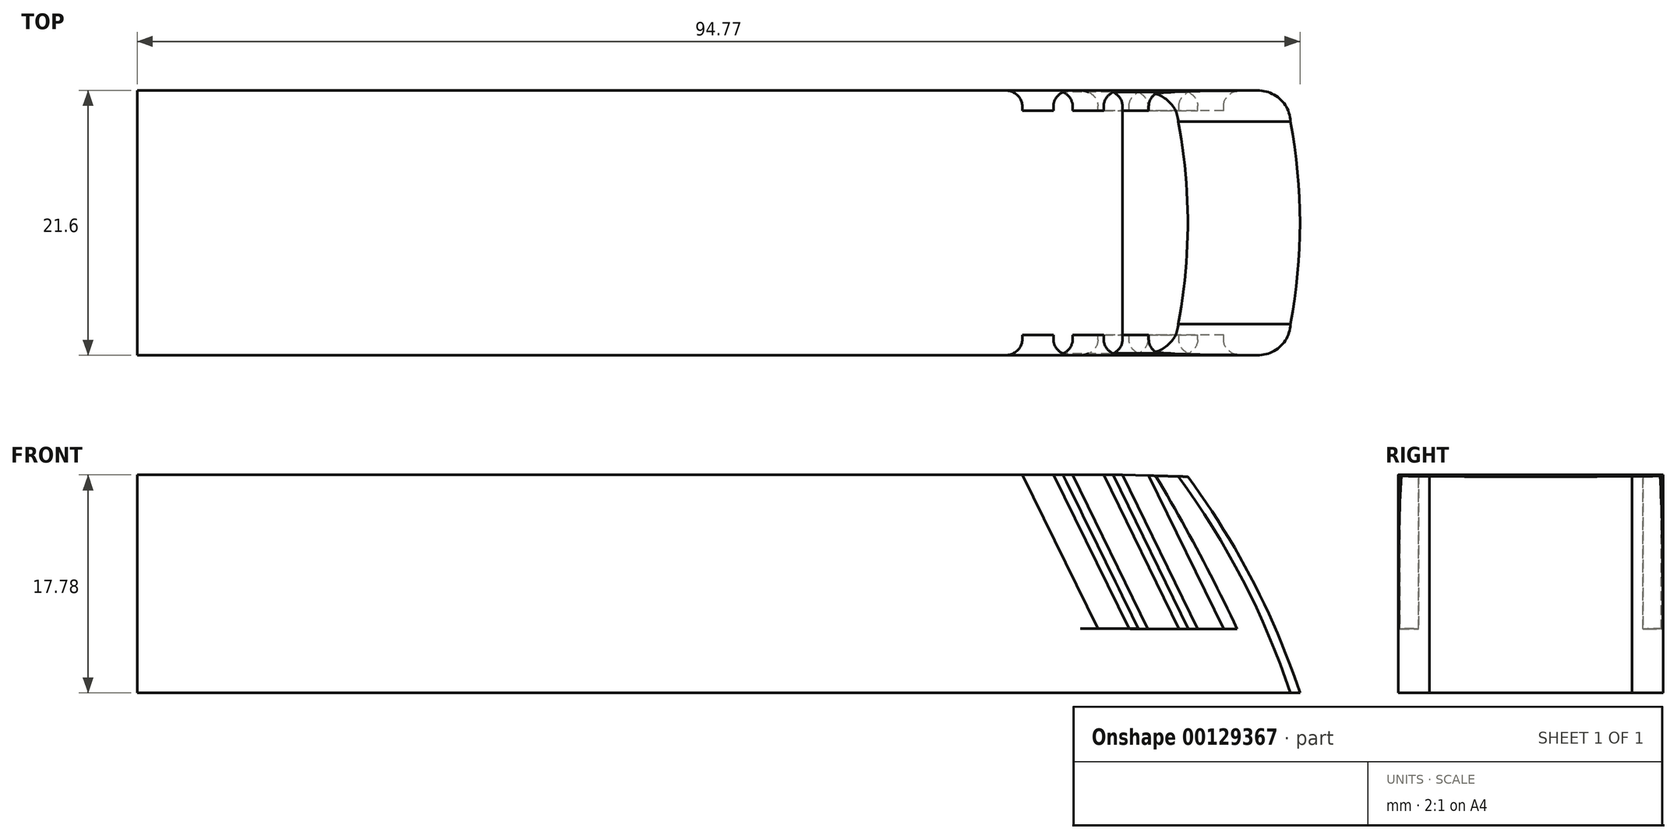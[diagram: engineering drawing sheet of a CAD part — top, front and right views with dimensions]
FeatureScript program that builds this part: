
annotation { "Feature Type Name" : "Feature", "Feature Type Description" : "" }
export const myFeature = defineFeature(function(context is Context, id is Id, definition is map)
    precondition{}
    {
        {
            var Q0;
            Q0=qCreatedBy(makeId("Front.planeOp"),FACE);
            var sketch = newSketch(context, id + "F0", { "sketchPlane" : qUnion([Q0])});
            skLineSegment(sketch, "E0", {"start": v(-54.59, -17.6) * mm, "end": v(-54.59, 0.19) * mm});
            skLineSegment(sketch, "E1", {"start": v(-54.59, -17.6) * mm, "end": v(39.4, -17.6) * mm});
            skLineSegment(sketch, "E2", {"start": v(-54.59, 0.19) * mm, "end": v(25.72, 0.19) * mm});
            skLineSegment(sketch, "E3.0", {"start": v(33.96, -12.37) * mm, "end": v(27.71, 0.43) * mm});
            skLineSegment(sketch, "E4", {"start": v(25.72, 0.19) * mm, "end": v(31.84, -12.37) * mm});
            skLineSegment(sketch, "E5", {"start": v(33.96, -12.37) * mm, "end": v(31.84, -12.37) * mm});
            skLineSegment(sketch, "E6", {"start": v(24.2, 0.19) * mm, "end": v(30.32, -12.37) * mm});
            skLineSegment(sketch, "E7", {"start": v(30.32, -12.37) * mm, "end": v(27.78, -12.37) * mm});
            skLineSegment(sketch, "E8", {"start": v(27.78, -12.37) * mm, "end": v(21.65, 0.19) * mm});
            skLineSegment(sketch, "E9", {"start": v(20.1, 0.19) * mm, "end": v(26.26, -12.35) * mm});
            skLineSegment(sketch, "E10", {"start": v(17.55, 0.19) * mm, "end": v(23.72, -12.35) * mm});
            skLineSegment(sketch, "E11", {"start": v(26.26, -12.35) * mm, "end": v(23.72, -12.35) * mm});
            skLineSegment(sketch, "E12", {"start": v(30.25, 0.06) * mm, "end": v(25.72, 0.19) * mm});
            skLineSegment(sketch, "E13", {"start": v(30.25, 0.06) * mm, "end": v(39.4, -17.6) * mm});
            skArc(sketch, "E14", {"start": v(39.4, -17.6) * mm, "mid": v(35.52, -8.4) * mm, "end": v(30.25, 0.06) * mm});
            skSolve(sketch);
        }
        {
            var Q0;
            {var subQ6=sQuery(id+"F0.wireOp",EDGE,"E0");Q0=makeQuery(id+"F0.imprint","IMPRINT",FACE,{"disambiguationData":[TD([[makeQuery(id+"F0.imprint","IMPRINT",EDGE,{"derivedFrom":subQ6}),-1.0]])]});}
            var Q1;
            Q1=makeQuery(id+"F0.imprint","IMPRINT",FACE,{"disambiguationData":[TD([[makeQuery(id+"F0.imprint","IMPRINT",EDGE,{"derivedFrom":sQuery(id+"F0.wireOp",EDGE,"657433ce-35f6-41b5-b99d-85d71bb0a3c1")}),-1.0]])]});
            var Q2;
            Q2=makeQuery(id+"F0.imprint","IMPRINT",FACE,{"disambiguationData":[TD([[makeQuery(id+"F0.imprint","IMPRINT",EDGE,{"derivedFrom":sQuery(id+"F0.wireOp",EDGE,"E13")}),1.0]])]});
            extrude(context, id + "F1", {"entities" : qUnion([Q0, Q1, Q2]), "depth" : 21.59 * mm, "symmetric" : true});
        }
        {
            var Q0;
            {var subQ0=sQuery(id+"F0.wireOp",EDGE,"E9");Q0=makeQuery(id+"F0.imprint","IMPRINT",FACE,{"disambiguationData":[TD([[makeQuery(id+"F0.imprint","IMPRINT",EDGE,{"derivedFrom":subQ0}),-1.0]])]});}
            var Q1;
            {var subQ0=sQuery(id+"F0.wireOp",EDGE,"E6");Q1=makeQuery(id+"F0.imprint","IMPRINT",FACE,{"disambiguationData":[TD([[makeQuery(id+"F0.imprint","IMPRINT",EDGE,{"derivedFrom":subQ0}),-1.0]])]});}
            var Q2;
            {var subQ4=sQuery(id+"F0.wireOp",EDGE,"E4");Q2=makeQuery(id+"F0.imprint","IMPRINT",FACE,{"disambiguationData":[TD([[makeQuery(id+"F0.imprint","IMPRINT",EDGE,{"derivedFrom":subQ4}),1.0]])]});}
            extrude(context, id + "F2", {"entities" : qUnion([Q0, Q1, Q2]), "operationType" : NewBodyOperationType.ADD, "depth" : 18.29 * mm, "symmetric" : true});
        }
        {
            var Q0;
            Q0=makeQuery(id+"F1.opExtrude","CAP_EDGE",EDGE,{"disambiguationData":[OSD([sQuery(id+"F0.wireOp",EDGE,"E10")])],"isStart":false});
            var Q1;
            Q1=makeQuery(id+"F1.opExtrude","CAP_EDGE",EDGE,{"disambiguationData":[OSD([sQuery(id+"F0.wireOp",EDGE,"E9")])],"isStart":false});
            var Q2;
            Q2=makeQuery(id+"F1.opExtrude","CAP_EDGE",EDGE,{"disambiguationData":[OSD([sQuery(id+"F0.wireOp",EDGE,"E8")])],"isStart":false});
            var Q3;
            Q3=makeQuery(id+"F1.opExtrude","CAP_EDGE",EDGE,{"disambiguationData":[OSD([sQuery(id+"F0.wireOp",EDGE,"E6")])],"isStart":false});
            var Q4;
            Q4=makeQuery(id+"F1.opExtrude","CAP_EDGE",EDGE,{"disambiguationData":[OSD([sQuery(id+"F0.wireOp",EDGE,"657433ce-35f6-41b5-b99d-85d71bb0a3c1")])],"isStart":false});
            var Q5;
            Q5=makeQuery(id+"F1.opExtrude","CAP_EDGE",EDGE,{"disambiguationData":[OSD([sQuery(id+"F0.wireOp",EDGE,"E3.0")])],"isStart":false});
            fillet(context, id + "F3", {"entities" : qUnion([Q0, Q1, Q2, Q3, Q4, Q5]), "radius" : 1.27 * mm, "tangentPropagation" : true, "allowEdgeOverflow" : false});
        }
        {
            var Q0;
            {var subQ0=sQuery(id+"F0.wireOp",EDGE,"E6");Q0=makeQuery(id+"F3.opFillet","BLEND_EDGE",EDGE,{"blendedFrom":[makeQuery(id+"F1.opExtrude","CAP_EDGE",EDGE,{"disambiguationData":[OSD([subQ0])],"isStart":false}),makeQuery(id+"F1.opExtrude","CAP_FACE",FACE,{"disambiguationData":[OSD([sQuery(id+"F0.wireOp",EDGE,"E0"),sQuery(id+"F0.wireOp",EDGE,"E1"),sQuery(id+"F0.wireOp",EDGE,"E2"),sQuery(id+"F0.wireOp",EDGE,"E3.0"),sQuery(id+"F0.wireOp",EDGE,"E4"),sQuery(id+"F0.wireOp",EDGE,"E5"),subQ0,sQuery(id+"F0.wireOp",EDGE,"E7"),sQuery(id+"F0.wireOp",EDGE,"E8"),sQuery(id+"F0.wireOp",EDGE,"E9"),sQuery(id+"F0.wireOp",EDGE,"E10"),sQuery(id+"F0.wireOp",EDGE,"E11"),sQuery(id+"F0.wireOp",EDGE,"657433ce-35f6-41b5-b99d-85d71bb0a3c1"),sQuery(id+"F0.wireOp",EDGE,"E12")])],"isStart":false})],"blendedInto":[makeQuery(id+"F1.opExtrude","CAP_FACE",FACE,{"disambiguationData":[OSD([sQuery(id+"F0.wireOp",EDGE,"E0"),sQuery(id+"F0.wireOp",EDGE,"E1"),sQuery(id+"F0.wireOp",EDGE,"E2"),sQuery(id+"F0.wireOp",EDGE,"E3.0"),sQuery(id+"F0.wireOp",EDGE,"E4"),sQuery(id+"F0.wireOp",EDGE,"E5"),subQ0,sQuery(id+"F0.wireOp",EDGE,"E7"),sQuery(id+"F0.wireOp",EDGE,"E8"),sQuery(id+"F0.wireOp",EDGE,"E9"),sQuery(id+"F0.wireOp",EDGE,"E10"),sQuery(id+"F0.wireOp",EDGE,"E11"),sQuery(id+"F0.wireOp",EDGE,"657433ce-35f6-41b5-b99d-85d71bb0a3c1"),sQuery(id+"F0.wireOp",EDGE,"E12")])],"isStart":false})]});}
            var Q1;
            Q1=makeQuery(id+"F1.opExtrude","CAP_EDGE",EDGE,{"disambiguationData":[OSD([sQuery(id+"F0.wireOp",EDGE,"E4")])],"isStart":false});
            fillet(context, id + "F4", {"entities" : qUnion([Q0, Q1]), "radius" : 1.27 * mm, "tangentPropagation" : true, "allowEdgeOverflow" : false});
        }
        {
            var Q0;
            Q0=makeQuery(id+"F1.opExtrude","CAP_EDGE",EDGE,{"disambiguationData":[OSD([sQuery(id+"F0.wireOp",EDGE,"E10")])],"isStart":true});
            var Q1;
            Q1=makeQuery(id+"F1.opExtrude","CAP_EDGE",EDGE,{"disambiguationData":[OSD([sQuery(id+"F0.wireOp",EDGE,"E9")])],"isStart":true});
            var Q2;
            Q2=makeQuery(id+"F1.opExtrude","CAP_EDGE",EDGE,{"disambiguationData":[OSD([sQuery(id+"F0.wireOp",EDGE,"E6")])],"isStart":true});
            var Q3;
            Q3=makeQuery(id+"F1.opExtrude","CAP_EDGE",EDGE,{"disambiguationData":[OSD([sQuery(id+"F0.wireOp",EDGE,"E3.0")])],"isStart":true});
            var Q4;
            Q4=makeQuery(id+"F1.opExtrude","CAP_EDGE",EDGE,{"disambiguationData":[OSD([sQuery(id+"F0.wireOp",EDGE,"657433ce-35f6-41b5-b99d-85d71bb0a3c1")])],"isStart":true});
            fillet(context, id + "F5", {"entities" : qUnion([Q0, Q1, Q2, Q3, Q4]), "radius" : 1.27 * mm, "tangentPropagation" : true, "allowEdgeOverflow" : false});
        }
        {
            var Q0;
            {var subQ0=sQuery(id+"F0.wireOp",EDGE,"E6");Q0=makeQuery(id+"F5.opFillet","BLEND_EDGE",EDGE,{"blendedFrom":[makeQuery(id+"F1.opExtrude","CAP_EDGE",EDGE,{"disambiguationData":[OSD([subQ0])],"isStart":true}),makeQuery(id+"F1.opExtrude","CAP_FACE",FACE,{"disambiguationData":[OSD([sQuery(id+"F0.wireOp",EDGE,"E0"),sQuery(id+"F0.wireOp",EDGE,"E1"),sQuery(id+"F0.wireOp",EDGE,"E2"),sQuery(id+"F0.wireOp",EDGE,"E3.0"),sQuery(id+"F0.wireOp",EDGE,"E4"),sQuery(id+"F0.wireOp",EDGE,"E5"),subQ0,sQuery(id+"F0.wireOp",EDGE,"E7"),sQuery(id+"F0.wireOp",EDGE,"E8"),sQuery(id+"F0.wireOp",EDGE,"E9"),sQuery(id+"F0.wireOp",EDGE,"E10"),sQuery(id+"F0.wireOp",EDGE,"E11"),sQuery(id+"F0.wireOp",EDGE,"657433ce-35f6-41b5-b99d-85d71bb0a3c1"),sQuery(id+"F0.wireOp",EDGE,"E12")])],"isStart":true})],"blendedInto":[makeQuery(id+"F1.opExtrude","CAP_FACE",FACE,{"disambiguationData":[OSD([sQuery(id+"F0.wireOp",EDGE,"E0"),sQuery(id+"F0.wireOp",EDGE,"E1"),sQuery(id+"F0.wireOp",EDGE,"E2"),sQuery(id+"F0.wireOp",EDGE,"E3.0"),sQuery(id+"F0.wireOp",EDGE,"E4"),sQuery(id+"F0.wireOp",EDGE,"E5"),subQ0,sQuery(id+"F0.wireOp",EDGE,"E7"),sQuery(id+"F0.wireOp",EDGE,"E8"),sQuery(id+"F0.wireOp",EDGE,"E9"),sQuery(id+"F0.wireOp",EDGE,"E10"),sQuery(id+"F0.wireOp",EDGE,"E11"),sQuery(id+"F0.wireOp",EDGE,"657433ce-35f6-41b5-b99d-85d71bb0a3c1"),sQuery(id+"F0.wireOp",EDGE,"E12")])],"isStart":true})]});}
            var Q1;
            Q1=makeQuery(id+"F1.opExtrude","CAP_EDGE",EDGE,{"disambiguationData":[OSD([sQuery(id+"F0.wireOp",EDGE,"E4")])],"isStart":true});
            var Q2;
            Q2=makeQuery(id+"F1.opExtrude","CAP_EDGE",EDGE,{"disambiguationData":[OSD([sQuery(id+"F0.wireOp",EDGE,"E8")])],"isStart":true});
            var Q3;
            {var subQ0=sQuery(id+"F0.wireOp",EDGE,"E9");Q3=makeQuery(id+"F5.opFillet","BLEND_EDGE",EDGE,{"blendedFrom":[makeQuery(id+"F1.opExtrude","CAP_EDGE",EDGE,{"disambiguationData":[OSD([subQ0])],"isStart":true}),makeQuery(id+"F1.opExtrude","CAP_FACE",FACE,{"disambiguationData":[OSD([sQuery(id+"F0.wireOp",EDGE,"E0"),sQuery(id+"F0.wireOp",EDGE,"E1"),sQuery(id+"F0.wireOp",EDGE,"E2"),sQuery(id+"F0.wireOp",EDGE,"E3.0"),sQuery(id+"F0.wireOp",EDGE,"E4"),sQuery(id+"F0.wireOp",EDGE,"E5"),sQuery(id+"F0.wireOp",EDGE,"E6"),sQuery(id+"F0.wireOp",EDGE,"E7"),sQuery(id+"F0.wireOp",EDGE,"E8"),subQ0,sQuery(id+"F0.wireOp",EDGE,"E10"),sQuery(id+"F0.wireOp",EDGE,"E11"),sQuery(id+"F0.wireOp",EDGE,"657433ce-35f6-41b5-b99d-85d71bb0a3c1"),sQuery(id+"F0.wireOp",EDGE,"E12")])],"isStart":true})],"blendedInto":[makeQuery(id+"F1.opExtrude","CAP_FACE",FACE,{"disambiguationData":[OSD([sQuery(id+"F0.wireOp",EDGE,"E0"),sQuery(id+"F0.wireOp",EDGE,"E1"),sQuery(id+"F0.wireOp",EDGE,"E2"),sQuery(id+"F0.wireOp",EDGE,"E3.0"),sQuery(id+"F0.wireOp",EDGE,"E4"),sQuery(id+"F0.wireOp",EDGE,"E5"),sQuery(id+"F0.wireOp",EDGE,"E6"),sQuery(id+"F0.wireOp",EDGE,"E7"),sQuery(id+"F0.wireOp",EDGE,"E8"),subQ0,sQuery(id+"F0.wireOp",EDGE,"E10"),sQuery(id+"F0.wireOp",EDGE,"E11"),sQuery(id+"F0.wireOp",EDGE,"657433ce-35f6-41b5-b99d-85d71bb0a3c1"),sQuery(id+"F0.wireOp",EDGE,"E12")])],"isStart":true})]});}
            fillet(context, id + "F6", {"entities" : qUnion([Q0, Q1, Q2, Q3]), "radius" : 1.27 * mm, "tangentPropagation" : true, "allowEdgeOverflow" : false});
        }
        {
            var Q0;
            Q0=makeQuery(id+"F1.opExtrude","CAP_EDGE",EDGE,{"disambiguationData":[OSD([sQuery(id+"F0.wireOp",EDGE,"E14")])],"isStart":false});
            var Q1;
            Q1=makeQuery(id+"F1.opExtrude","CAP_EDGE",EDGE,{"disambiguationData":[OSD([sQuery(id+"F0.wireOp",EDGE,"E14")])],"isStart":true});
            fillet(context, id + "F7", {"entities" : qUnion([Q0, Q1]), "radius" : 2.54 * mm, "allowEdgeOverflow" : false});
        }
        {
            var Q0;
            {var subQ0=sQuery(id+"F0.wireOp",EDGE,"E12");Q0=makeQuery(id+"F2.boolean.opBoolean","MERGE",FACE,{"derivedFrom":[makeQuery(id+"F1.opExtrude","SWEPT_FACE",FACE,{"disambiguationData":[OSD([subQ0])]}),makeQuery(id+"F2.opExtrude","SWEPT_FACE",FACE,{"disambiguationData":[OSD([subQ0])]})]});}
            cPlane(context, id + "F8", {"entities" : qUnion([Q0]), "cplaneType" : CPlaneType.OFFSET, "offset" : 0 * mm, "width" : 152.4 * mm, "height" : 152.4 * mm});
        }
        {
            var Q0;
            Q0=qCreatedBy(id+"F8.planeOp",FACE);
            var sketch = newSketch(context, id + "F9", { "sketchPlane" : qUnion([Q0])});
            skLineSegment(sketch, "E15", {"start": v(30.24, 8.26) * mm, "end": v(30.24, -8.26) * mm});
            skArc(sketch, "E16", {"start": v(30.24, -8.26) * mm, "mid": v(31.03, 0) * mm, "end": v(30.24, 8.26) * mm});
            skSolve(sketch);
        }
        {
            var Q0;
            Q0=makeQuery(id+"F1.opExtrude","SWEPT_FACE",FACE,{"disambiguationData":[OSD([sQuery(id+"F0.wireOp",EDGE,"E1")])]});
            cPlane(context, id + "F10", {"entities" : qUnion([Q0]), "cplaneType" : CPlaneType.OFFSET, "offset" : 0 * mm, "width" : 152.4 * mm, "height" : 152.4 * mm});
        }
        {
            var Q0;
            Q0=qCreatedBy(id+"F10.planeOp",FACE);
            var sketch = newSketch(context, id + "F11", { "sketchPlane" : qUnion([Q0])});
            skLineSegment(sketch, "E17", {"start": v(39.4, 8.26) * mm, "end": v(39.4, -8.26) * mm});
            skArc(sketch, "E18", {"start": v(39.4, -8.25) * mm, "mid": v(40.18, 0) * mm, "end": v(39.4, 8.25) * mm});
            skSolve(sketch);
        }
        {
            var Q1;
            Q1=makeQuery(id+"F9.imprint","IMPRINT",FACE,{"disambiguationData":[TD([[makeQuery(id+"F9.imprint","IMPRINT",EDGE,{"derivedFrom":sQuery(id+"F9.wireOp",EDGE,"E15")}),1.0]])]});
            var Q2;
            Q2=makeQuery(id+"F11.imprint","IMPRINT",FACE,{"disambiguationData":[TD([[makeQuery(id+"F11.imprint","IMPRINT",EDGE,{"derivedFrom":sQuery(id+"F11.wireOp",EDGE,"E17")}),1.0]])]});
            var Q3;
            {var subQ0=sQuery(id+"F0.wireOp",EDGE,"E14");Q3=makeQuery(id+"F7.opFillet","BLEND_EDGE",EDGE,{"blendedFrom":[makeQuery(id+"F1.opExtrude","CAP_EDGE",EDGE,{"disambiguationData":[OSD([subQ0])],"isStart":false}),makeQuery(id+"F1.opExtrude","SWEPT_FACE",FACE,{"disambiguationData":[OSD([subQ0])]})],"blendedInto":[makeQuery(id+"F1.opExtrude","SWEPT_FACE",FACE,{"disambiguationData":[OSD([subQ0])]})]});}
            var Q4;
            {var subQ0=sQuery(id+"F0.wireOp",EDGE,"E14");Q4=makeQuery(id+"F7.opFillet","BLEND_EDGE",EDGE,{"blendedFrom":[makeQuery(id+"F1.opExtrude","CAP_EDGE",EDGE,{"disambiguationData":[OSD([subQ0])],"isStart":true}),makeQuery(id+"F1.opExtrude","SWEPT_FACE",FACE,{"disambiguationData":[OSD([subQ0])]})],"blendedInto":[makeQuery(id+"F1.opExtrude","SWEPT_FACE",FACE,{"disambiguationData":[OSD([subQ0])]})]});}
            loft(context, id + "F12", {"operationType" : NewBodyOperationType.ADD, "addGuides" : true, "sheetProfilesArray" : [{ "sheetProfileEntities" : qUnion([Q1]) }, { "sheetProfileEntities" : qUnion([Q2]) }], "guidesArray" : [{ "guideEntities" : qUnion([Q3]), "guideDerivativeType" : LoftGuideDerivativeType.DEFAULT, "guideDerivativeMagnitude" : 1 }, { "guideEntities" : qUnion([Q4]), "guideDerivativeType" : LoftGuideDerivativeType.DEFAULT, "guideDerivativeMagnitude" : 1 }]});
        }
    });
